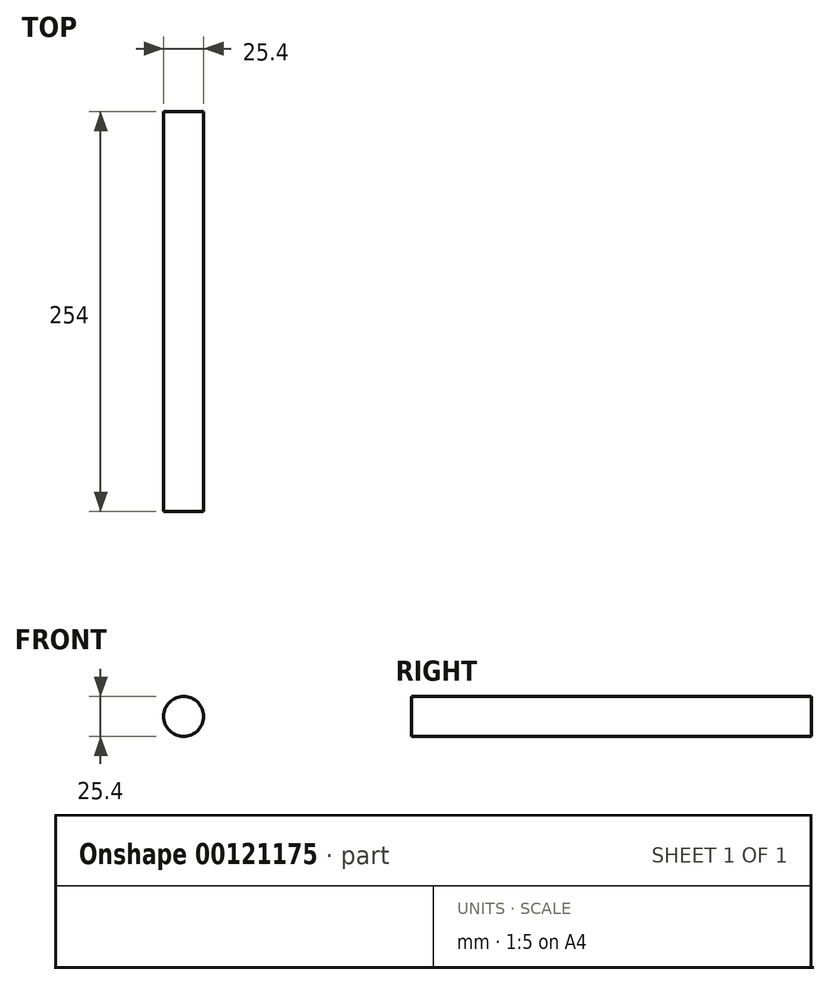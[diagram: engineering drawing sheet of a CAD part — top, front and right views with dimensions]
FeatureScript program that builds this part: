
annotation { "Feature Type Name" : "Feature", "Feature Type Description" : "" }
export const myFeature = defineFeature(function(context is Context, id is Id, definition is map)
    precondition{}
    {
        {
            var Q0;
            Q0=qCreatedBy(makeId("Front.planeOp"),FACE);
            var sketch = newSketch(context, id + "F0", { "sketchPlane" : qUnion([Q0])});
            skCircle(sketch, "E0", {"center": v(0, 0) * mm, "radius": 12.7 * mm});
            skSolve(sketch);
        }
        {
            var Q0;
            Q0 = qSketchRegion(id + "F0", true);
            extrude(context, id + "F1", {"entities" : qUnion([Q0]), "depth" : 254 * mm});
        }
    });
